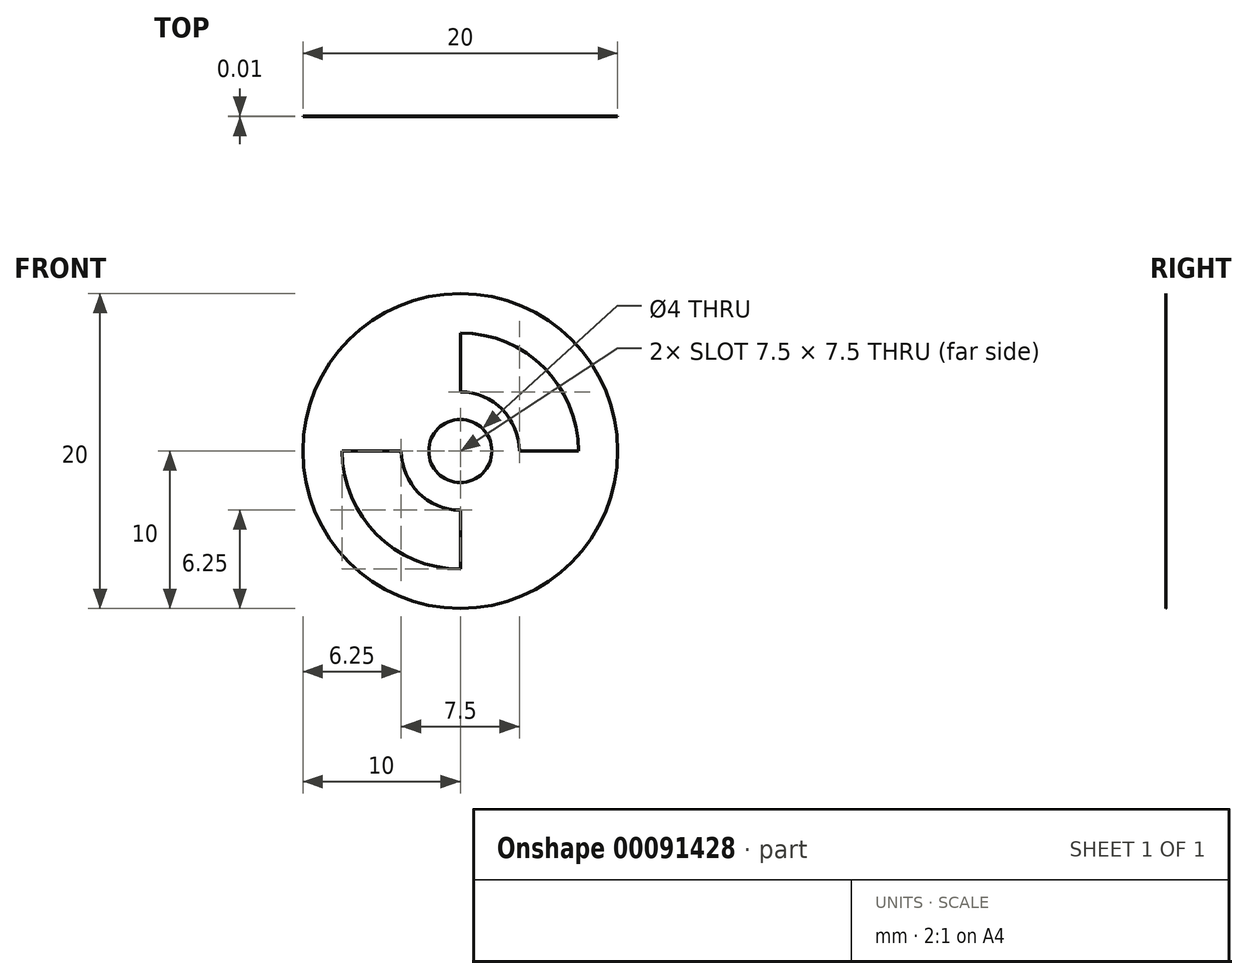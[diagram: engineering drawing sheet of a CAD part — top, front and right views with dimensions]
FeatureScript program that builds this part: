
annotation { "Feature Type Name" : "Feature", "Feature Type Description" : "" }
export const myFeature = defineFeature(function(context is Context, id is Id, definition is map)
    precondition{}
    {
        {
            var Q0;
            Q0=qCreatedBy(makeId("Front.planeOp"),FACE);
            var sketch = newSketch(context, id + "F0", { "sketchPlane" : qUnion([Q0])});
            skCircle(sketch, "E0", {"center": v(0, 0) * mm, "radius": 10 * mm});
            skCircle(sketch, "E1", {"center": v(0, 0) * mm, "radius": 2 * mm});
            skCircle(sketch, "E2", {"center": v(0, 0) * mm, "radius": 7.5 * mm});
            skCircle(sketch, "E3", {"center": v(0, 0) * mm, "radius": 3.75 * mm});
            skLineSegment(sketch, "E4", {"start": v(-3.75, 0) * mm, "end": v(-7.5, 0) * mm});
            skLineSegment(sketch, "E5", {"start": v(0, 7.5) * mm, "end": v(0, 3.75) * mm});
            skLineSegment(sketch, "E6", {"start": v(0, -3.75) * mm, "end": v(0, -7.5) * mm});
            skLineSegment(sketch, "E7", {"start": v(3.75, 0) * mm, "end": v(7.5, 0) * mm});
            skSolve(sketch);
        }
        {
            var Q0;
            Q0 = qSketchRegion(id + "F0", true);
            var Q1;
            {var subQ0=sQuery(id+"F0.wireOp",EDGE,"E6");Q1=makeQuery(id+"F0.imprint","IMPRINT",FACE,{"disambiguationData":[TD([[makeQuery(id+"F0.imprint","IMPRINT",EDGE,{"derivedFrom":subQ0}),1.0]])]});}
            var Q2;
            {var subQ0=sQuery(id+"F0.wireOp",EDGE,"E4");Q2=makeQuery(id+"F0.imprint","IMPRINT",FACE,{"disambiguationData":[TD([[makeQuery(id+"F0.imprint","IMPRINT",EDGE,{"derivedFrom":subQ0}),-1.0]])]});}
            var Q3;
            Q3=makeQuery(id+"F0.imprint","IMPRINT",FACE,{"disambiguationData":[TD([[makeQuery(id+"F0.imprint","IMPRINT",EDGE,{"derivedFrom":sQuery(id+"F0.wireOp",EDGE,"E1")}),-1.0]])]});
            extrude(context, id + "F1", {"entities" : qUnion([Q0, Q1, Q2, Q3]), "depth" : 1 / 101.6 * mm});
        }
    });
